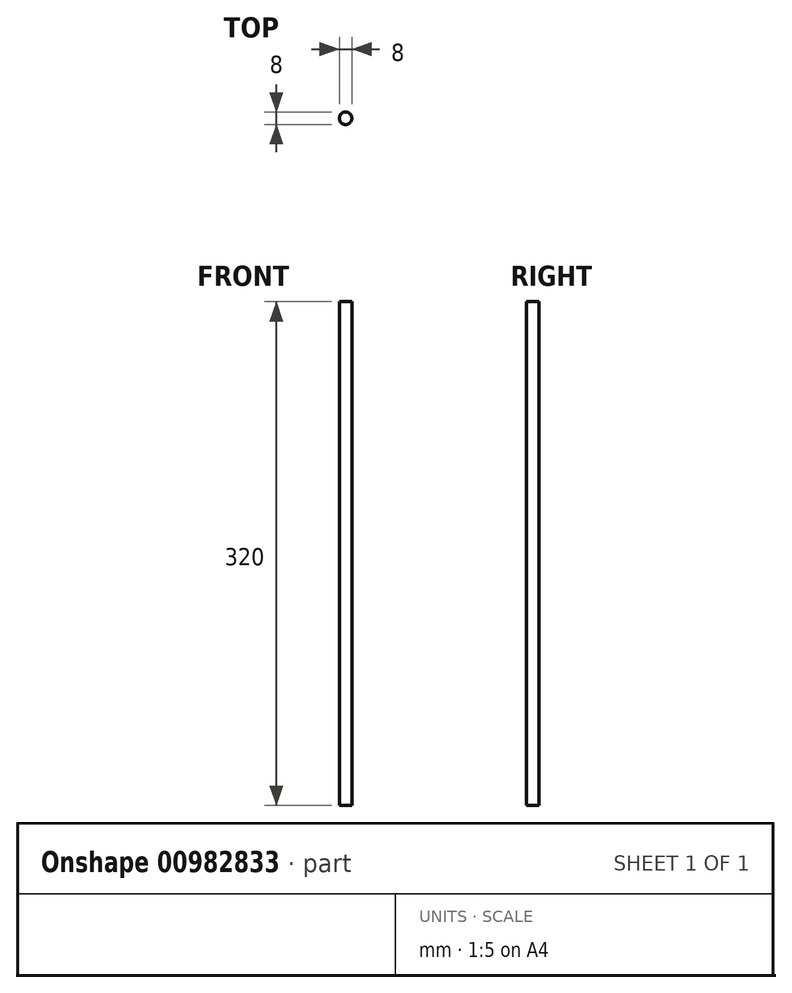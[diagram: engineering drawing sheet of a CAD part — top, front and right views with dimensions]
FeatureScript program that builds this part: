
annotation { "Feature Type Name" : "Feature", "Feature Type Description" : "" }
export const myFeature = defineFeature(function(context is Context, id is Id, definition is map)
    precondition{}
    {
        {
            var Q0;
            Q0=qCreatedBy(makeId("Top.planeOp"),FACE);
            var sketch = newSketch(context, id + "F0", { "sketchPlane" : qUnion([Q0])});
            skCircle(sketch, "E0", {"center": v(0, 0) * mm, "radius": 4 * mm});
            skSolve(sketch);
        }
        {
            var Q0;
            Q0 = qSketchRegion(id + "F0", true);
            extrude(context, id + "F1", {"entities" : qUnion([Q0]), "depth" : 320 * mm, "offsetDistance" : 25 * mm});
        }
    });
